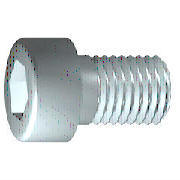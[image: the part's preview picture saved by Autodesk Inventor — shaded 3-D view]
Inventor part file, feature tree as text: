
AUTODESK INVENTOR PART (.ipt)
format: ipt  version: 2017 (Build 210142000, 142)  size: 190,976 bytes
history: native  units: mm (DEFAULTED — no unit token found)
features: sketch x2, extrude x1, plane x1, fillet x1
ambient origin geometry x7: Origin, YZ Plane, XY Plane, X Axis, Y Axis, Z Axis, Center Point
bodies: Solid1 (feature_tree), Body (feature_tree)
feature tree (5):
  extrude  "Slot"  Depth=3.0mm
  plane  "Work Plane1"
  fillet  "Fillet2"  Radius=3.0mm
  sketch  "Sketch1"  dims[d1=8.693275mm d2=0.306825mm d3=3.0mm]
  sketch  "Sketch2"  dims[d4=1.5mm d5=60.0deg d6=3.0mm d7=3.0mm d8=2.886751mm d9=5.5mm d10=90.0deg d11=10.0mm d12=0.0mm d13=8.693275mm d14=0.0mm d15=0.306725mm d16=0.306725mm d17=0.3mm d19=0.0mm d26=10.0mm d27=45.0deg d28=0.0mm d29=0.0mm d30=0.1mm]
